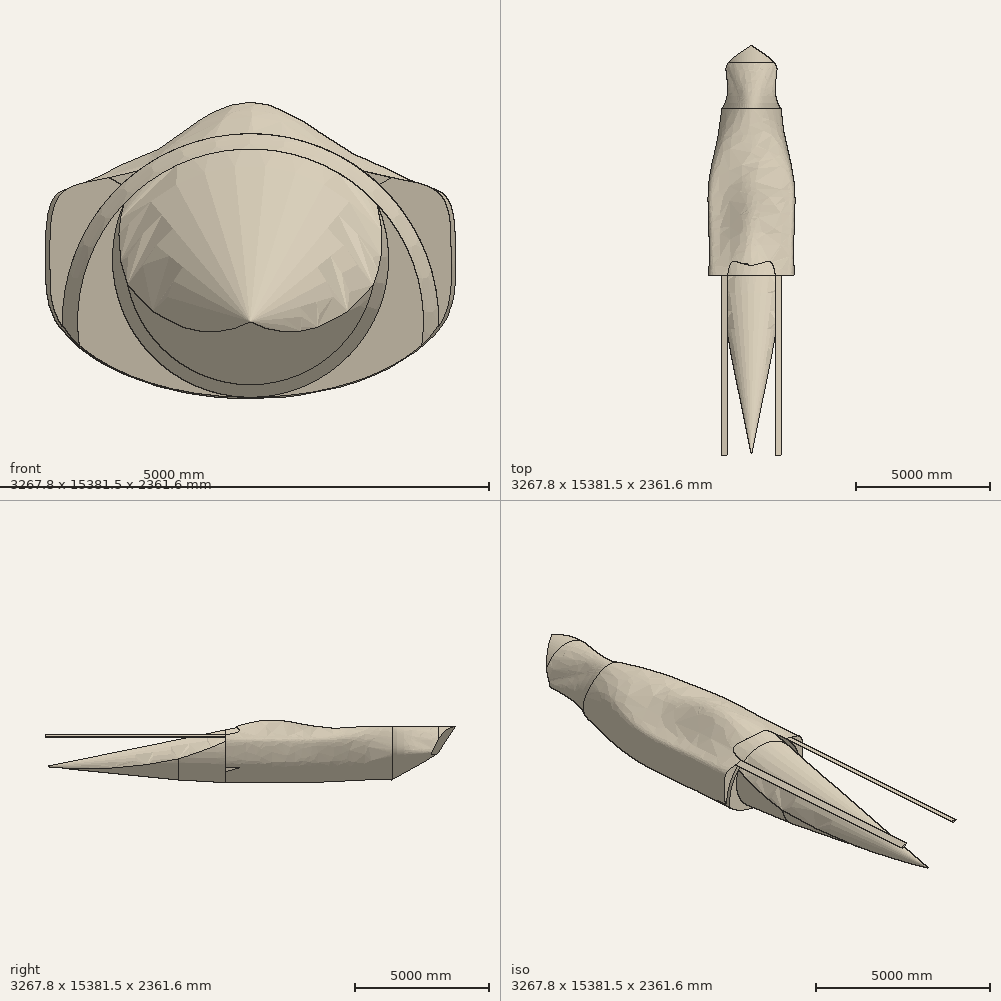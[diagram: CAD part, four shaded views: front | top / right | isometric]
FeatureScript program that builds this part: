
annotation { "Feature Type Name" : "Feature", "Feature Type Description" : "" }
export const myFeature = defineFeature(function(context is Context, id is Id, definition is map)
    precondition{}
    {
        {
            var Q0;
            Q0=qCreatedBy(makeId("Front.planeOp"),FACE);
            cPlane(context, id + "F0", {"entities" : qUnion([Q0]), "cplaneType" : CPlaneType.OFFSET, "offset" : 1750 * mm, "width" : 152.4 * mm, "height" : 152.4 * mm});
        }
        {
            var Q0;
            Q0=qCreatedBy(id+"F0.planeOp",FACE);
            var sketch = newSketch(context, id + "F1", { "sketchPlane" : qUnion([Q0])});
            skPoint(sketch, "E0.middle", {"position": v(0, 0) * mm});
            skFitSpline(sketch, "E1", {"points": [v(0, 877.87) * mm, v(1060, 662.5) * mm, v(1517.6, 506.84) * mm, v(1600, 0) * mm, v(1517.6, -506.84) * mm, v(750, -1000) * mm, v(-750, -1000) * mm, v(-1517.6, -506.84) * mm, v(-1600, 0) * mm, v(-1517.6, 506.84) * mm, v(-1060, 662.5) * mm, v(0, 877.87) * mm]});
            skSolve(sketch);
        }
        {
            var Q0;
            Q0=qCreatedBy(makeId("Front.planeOp"),FACE);
            var sketch = newSketch(context, id + "F2", { "sketchPlane" : qUnion([Q0])});
            skPoint(sketch, "E2.middle", {"position": v(0, 0) * mm});
            skFitSpline(sketch, "E3", {"points": [v(0, 1250) * mm, v(1060, 662.5) * mm, v(1517.6, 506.84) * mm, v(1600, 0) * mm, v(1517.6, -506.84) * mm, v(750, -1000) * mm, v(-750, -1000) * mm, v(-1517.6, -506.84) * mm, v(-1600, 0) * mm, v(-1517.6, 506.84) * mm, v(-1060, 662.5) * mm, v(0, 1250) * mm]});
            skSolve(sketch);
        }
        {
            var Q0;
            Q0=qCreatedBy(makeId("Front.planeOp"),FACE);
            cPlane(context, id + "F3", {"entities" : qUnion([Q0]), "cplaneType" : CPlaneType.OFFSET, "offset" : 1750 * mm, "oppositeDirection" : true, "width" : 150 * mm, "height" : 150 * mm});
        }
        {
            var Q0;
            Q0=qCreatedBy(id+"F3.planeOp",FACE);
            var sketch = newSketch(context, id + "F4", { "sketchPlane" : qUnion([Q0])});
            skPoint(sketch, "E4.middle", {"position": v(0, 0) * mm});
            skFitSpline(sketch, "E5", {"points": [v(0, 1000) * mm, v(1060, 662.5) * mm, v(1517.6, 506.84) * mm, v(1600, 0) * mm, v(1517.6, -506.84) * mm, v(750, -1000) * mm, v(-750, -1000) * mm, v(-1517.6, -506.84) * mm, v(-1600, 0) * mm, v(-1517.6, 506.84) * mm, v(-1060, 662.5) * mm, v(0, 1000) * mm]});
            skSolve(sketch);
        }
        {
            var Q0;
            Q0=qCreatedBy(makeId("Front.planeOp"),FACE);
            cPlane(context, id + "F5", {"entities" : qUnion([Q0]), "cplaneType" : CPlaneType.OFFSET, "offset" : 3500 * mm, "oppositeDirection" : true, "width" : 150 * mm, "height" : 150 * mm});
        }
        {
            var Q0;
            Q0=qCreatedBy(id+"F5.planeOp",FACE);
            var sketch = newSketch(context, id + "F6", { "sketchPlane" : qUnion([Q0])});
            skPoint(sketch, "E6.middle", {"position": v(0, 0) * mm});
            skFitSpline(sketch, "E7", {"points": [v(0, 1000) * mm, v(1060, 662.5) * mm, v(1250, 0) * mm, v(1060, -662.5) * mm, v(0, -1000) * mm, v(-1060, -662.5) * mm, v(-1250, 0) * mm, v(-1060, 662.5) * mm, v(0, 1000) * mm]});
            skSolve(sketch);
        }
        {
            var Q0;
            Q0=qCreatedBy(makeId("Front.planeOp"),FACE);
            cPlane(context, id + "F7", {"entities" : qUnion([Q0]), "cplaneType" : CPlaneType.OFFSET, "offset" : 4500 * mm, "oppositeDirection" : true, "width" : 150 * mm, "height" : 150 * mm});
        }
        {
            var Q0;
            Q0=qCreatedBy(id+"F7.planeOp",FACE);
            var sketch = newSketch(context, id + "F8", { "sketchPlane" : qUnion([Q0])});
            skPoint(sketch, "E8.middle", {"position": v(0, 0) * mm});
            skFitSpline(sketch, "E9", {"points": [v(0, 1000) * mm, v(848, 530) * mm, v(1108.5, 0) * mm, v(848, -530) * mm, v(0, -1000) * mm, v(-848, -530) * mm, v(-1108.5, 0) * mm, v(-848, 530) * mm, v(0, 1000) * mm]});
            skSolve(sketch);
        }
        {
            var Q0;
            Q0=qCreatedBy(makeId("Front.planeOp"),FACE);
            cPlane(context, id + "F9", {"entities" : qUnion([Q0]), "cplaneType" : CPlaneType.OFFSET, "offset" : 6232.05 * mm, "oppositeDirection" : true, "width" : 150 * mm, "height" : 150 * mm});
        }
        {
            var Q0;
            Q0=qCreatedBy(id+"F9.planeOp",FACE);
            var sketch = newSketch(context, id + "F10", { "sketchPlane" : qUnion([Q0])});
            skArc(sketch, "E10", {"start": v(998.61, 52.63) * mm, "mid": v(0, 1000) * mm, "end": v(-998.61, 52.63) * mm});
            skLineSegment(sketch, "E11", {"start": v(0, 0) * mm, "end": v(-948.68, 0) * mm});
            skLineSegment(sketch, "E12", {"start": v(0, 0) * mm, "end": v(948.68, 0) * mm});
            skPoint(sketch, "E13.visualSharp", {"position": v(-1000, 0) * mm});
            skArc(sketch, "E13.filletArc", {"start": v(-998.61, 52.63) * mm, "mid": v(-984.96, 15.59) * mm, "end": v(-948.68, 0) * mm});
            skPoint(sketch, "E14.visualSharp", {"position": v(1000, 0) * mm});
            skArc(sketch, "E14.filletArc", {"start": v(948.68, 0) * mm, "mid": v(984.96, 15.59) * mm, "end": v(998.61, 52.63) * mm});
            skSolve(sketch);
        }
        {
            var Q0;
            Q0=sQuery(id+"F10.wireOp",EDGE,"E11");
            var Q1;
            Q1=sQuery(id+"F8.wireOp",VERTEX,"E9.6.internal");
            cPlane(context, id + "F11", {"entities" : qUnion([Q0, Q1]), "cplaneType" : CPlaneType.LINE_ANGLE, "offset" : 25 * mm, "angle" : 0 * degree, "width" : 150 * mm, "height" : 150 * mm});
        }
        {
            var Q0;
            Q0=qCreatedBy(id+"F11.planeOp",FACE);
            var sketch = newSketch(context, id + "F12", { "sketchPlane" : qUnion([Q0])});
            skFitSpline(sketch, "E15", {"points": [v(-1108.5, 4500) * mm, v(-948.68, 6232.05) * mm], "startDerivative": vector(1200, 1755) * mm, "endDerivative": vector(158.07, 1422.55) * mm});
            skFitSpline(sketch, "E16", {"points": [v(1108.5, 4500) * mm, v(948.68, 6232.05) * mm], "startDerivative": vector(-1200, 1755) * mm, "endDerivative": vector(-158.07, 1422.55) * mm});
            skSolve(sketch);
        }
        {
            var Q0;
            Q0=makeQuery(id+"F1.imprint","IMPRINT",FACE,{"disambiguationData":[TD([[makeQuery(id+"F1.imprint","IMPRINT",EDGE,{"derivedFrom":sQuery(id+"F1.wireOp",EDGE,"E1")}),-1.0]])]});
            var Q1;
            Q1=makeQuery(id+"F2.imprint","IMPRINT",FACE,{"disambiguationData":[TD([[makeQuery(id+"F2.imprint","IMPRINT",EDGE,{"derivedFrom":sQuery(id+"F2.wireOp",EDGE,"E3")}),-1.0]])]});
            var Q2;
            Q2=makeQuery(id+"F4.imprint","IMPRINT",FACE,{"disambiguationData":[TD([[makeQuery(id+"F4.imprint","IMPRINT",EDGE,{"derivedFrom":sQuery(id+"F4.wireOp",EDGE,"E5")}),-1.0]])]});
            var Q3;
            Q3=makeQuery(id+"F6.imprint","IMPRINT",FACE,{"disambiguationData":[TD([[makeQuery(id+"F6.imprint","IMPRINT",EDGE,{"derivedFrom":sQuery(id+"F6.wireOp",EDGE,"E7")}),-1.0]])]});
            var Q4;
            Q4=makeQuery(id+"F8.imprint","IMPRINT",FACE,{"disambiguationData":[TD([[makeQuery(id+"F8.imprint","IMPRINT",EDGE,{"derivedFrom":sQuery(id+"F8.wireOp",EDGE,"E9")}),-1.0]])]});
            loft(context, id + "F13", {"sheetProfilesArray" : [{ "sheetProfileEntities" : qUnion([Q0]) }, { "sheetProfileEntities" : qUnion([Q1]) }, { "sheetProfileEntities" : qUnion([Q2]) }, { "sheetProfileEntities" : qUnion([Q3]) }, { "sheetProfileEntities" : qUnion([Q4]) }]});
        }
        {
            var Q1;
            Q1=makeQuery(id+"F8.imprint","IMPRINT",FACE,{"disambiguationData":[TD([[makeQuery(id+"F8.imprint","IMPRINT",EDGE,{"derivedFrom":sQuery(id+"F8.wireOp",EDGE,"E9")}),-1.0]])]});
            var Q2;
            Q2=makeQuery(id+"F10.imprint","IMPRINT",FACE,{"disambiguationData":[TD([[makeQuery(id+"F10.imprint","IMPRINT",EDGE,{"derivedFrom":sQuery(id+"F10.wireOp",EDGE,"E10")}),1.0]])]});
            var Q3;
            Q3=sQuery(id+"F12.wireOp",EDGE,"E15");
            var Q4;
            Q4=sQuery(id+"F12.wireOp",EDGE,"E16");
            loft(context, id + "F14", {"operationType" : NewBodyOperationType.ADD, "addGuides" : true, "sheetProfilesArray" : [{ "sheetProfileEntities" : qUnion([Q1]) }, { "sheetProfileEntities" : qUnion([Q2]) }], "guidesArray" : [{ "guideEntities" : qUnion([Q3]), "guideDerivativeType" : LoftGuideDerivativeType.DEFAULT, "guideDerivativeMagnitude" : 1 }, { "guideEntities" : qUnion([Q4]), "guideDerivativeType" : LoftGuideDerivativeType.DEFAULT, "guideDerivativeMagnitude" : 1 }]});
        }
        {
            var Q0;
            Q0 = qSketchRegion(id + "F1", true);
            extrude(context, id + "F15", {"entities" : qUnion([Q0]), "depth" : 6750 * mm});
        }
        {
            var Q0;
            Q0=qCreatedBy(makeId("Right.planeOp"),FACE);
            var sketch = newSketch(context, id + "F16", { "sketchPlane" : qUnion([Q0])});
            skLineSegment(sketch, "E17", {"start": v(0, 0) * mm, "end": v(-3500, 0) * mm});
            skLineSegment(sketch, "E18", {"start": v(-3500, 0) * mm, "end": v(-3500, -1000) * mm});
            skLineSegment(sketch, "E19", {"start": v(-3500, -1000) * mm, "end": v(-8500, -1000) * mm});
            skLineSegment(sketch, "E20", {"start": v(-8500, -1000) * mm, "end": v(-8500, -499.31) * mm});
            skLineSegment(sketch, "E21", {"start": v(-1151.4, 0) * mm, "end": v(-1151.4, 1000) * mm});
            skLineSegment(sketch, "E22", {"start": v(-1151.4, 1000) * mm, "end": v(-8500, -499.31) * mm});
            skLineSegment(sketch, "E23", {"start": v(-8500, -499.31) * mm, "end": v(-3500, -1000) * mm});
            skLineSegment(sketch, "E24", {"start": v(-3500, 1000) * mm, "end": v(4500, 1000) * mm});
            skLineSegment(sketch, "E25", {"start": v(-3500, 1000) * mm, "end": v(-8500, 1000) * mm});
            skLineSegment(sketch, "E26", {"start": v(-8500, 1000) * mm, "end": v(-8500, -499.31) * mm});
            skLineSegment(sketch, "E27", {"start": v(-8500, -1000) * mm, "end": v(-8500, -1750) * mm});
            skLineSegment(sketch, "E28", {"start": v(-8500, -1750) * mm, "end": v(-1750, -1750) * mm});
            skPoint(sketch, "E28.endSnap0", {"position": v(-1750, 0) * mm});
            skLineSegment(sketch, "E29", {"start": v(-1750, 0) * mm, "end": v(-1750, -1099.92) * mm});
            skLineSegment(sketch, "E30", {"start": v(-1750, -1099.92) * mm, "end": v(-3500, -1000) * mm});
            skLineSegment(sketch, "E31", {"start": v(-1750, -1099.92) * mm, "end": v(-1750, -1750) * mm});
            skLineSegment(sketch, "E32", {"start": v(-8500, -499.31) * mm, "end": v(-3500, -499.31) * mm});
            skSolve(sketch);
        }
        {
            var Q0;
            {var subQ0=sQuery(id+"F16.wireOp",EDGE,"E22");Q0=makeQuery(id+"F16.imprint","IMPRINT",FACE,{"disambiguationData":[TD([[makeQuery(id+"F16.imprint","IMPRINT",EDGE,{"derivedFrom":subQ0}),-1.0]])]});}
            var Q1;
            Q1=sQuery(id+"F16.wireOp",EDGE,"E32");
            revolve(context, id + "F17", {"operationType" : NewBodyOperationType.REMOVE, "entities" : qUnion([Q0]), "axis" : qUnion([Q1]), "revolveType" : RevolveType.SYMMETRIC, "oppositeDirection" : true, "angle" : 250 * degree});
        }
        {
            var Q0;
            Q0=makeQuery(id+"F16.imprint","IMPRINT",FACE,{"disambiguationData":[TD([[makeQuery(id+"F16.imprint","IMPRINT",EDGE,{"derivedFrom":sQuery(id+"F16.wireOp",EDGE,"E19")}),-1.0]])]});
            var Q1;
            Q1=makeQuery(id+"F16.imprint","IMPRINT",FACE,{"disambiguationData":[TD([[makeQuery(id+"F16.imprint","IMPRINT",EDGE,{"derivedFrom":sQuery(id+"F16.wireOp",EDGE,"E19")}),1.0]])]});
            var Q2;
            Q2=sQuery(id+"F16.wireOp",EDGE,"E17");
            revolve(context, id + "F18", {"operationType" : NewBodyOperationType.REMOVE, "entities" : qUnion([Q0, Q1]), "axis" : qUnion([Q2]), "revolveType" : RevolveType.SYMMETRIC, "oppositeDirection" : true, "angle" : 240 * degree});
        }
        {
            var Q0;
            Q0=makeQuery(id+"F14.opLoft","CAP_FACE",FACE,{"disambiguationData":[OSD([makeQuery(id+"F10.imprint","IMPRINT",FACE,{"disambiguationData":[TD([[makeQuery(id+"F10.imprint","IMPRINT",EDGE,{"derivedFrom":sQuery(id+"F10.wireOp",EDGE,"E10")}),1.0]])]})])],"isStart":true});
            extrude(context, id + "F19", {"entities" : qUnion([Q0]), "operationType" : NewBodyOperationType.ADD, "depth" : 649.4 * mm});
        }
        {
            var Q0;
            Q0=qCreatedBy(makeId("Right.planeOp"),FACE);
            var sketch = newSketch(context, id + "F20", { "sketchPlane" : qUnion([Q0])});
            skLineSegment(sketch, "E33", {"start": v(0, 0) * mm, "end": v(4500, 0) * mm});
            skLineSegment(sketch, "E34", {"start": v(4500, 0) * mm, "end": v(6232.05, 0) * mm});
            skLineSegment(sketch, "E35", {"start": v(4500, 0) * mm, "end": v(4500, 1000) * mm});
            skLineSegment(sketch, "E36", {"start": v(4500, 1000) * mm, "end": v(6881.46, 1000) * mm});
            skLineSegment(sketch, "E37", {"start": v(6881.46, 1000) * mm, "end": v(6881.46, -1000) * mm});
            skLineSegment(sketch, "E38", {"start": v(6881.46, 1000) * mm, "end": v(6232.05, 0) * mm});
            skLineSegment(sketch, "E39", {"start": v(6232.05, 0) * mm, "end": v(5582.64, -1000) * mm});
            skLineSegment(sketch, "E40", {"start": v(5582.64, -1000) * mm, "end": v(6881.46, -1000) * mm});
            skSolve(sketch);
        }
        {
            var Q0;
            Q0=makeQuery(id+"F20.imprint","IMPRINT",FACE,{"disambiguationData":[TD([[makeQuery(id+"F20.imprint","IMPRINT",EDGE,{"derivedFrom":sQuery(id+"F20.wireOp",EDGE,"E37")}),-1.0]])]});
            var Q1;
            Q1=sQuery(id+"F20.wireOp",EDGE,"E36");
            revolve(context, id + "F21", {"operationType" : NewBodyOperationType.REMOVE, "entities" : qUnion([Q0]), "axis" : qUnion([Q1]), "revolveType" : RevolveType.SYMMETRIC, "oppositeDirection" : true, "angle" : 182 * degree});
        }
    });
